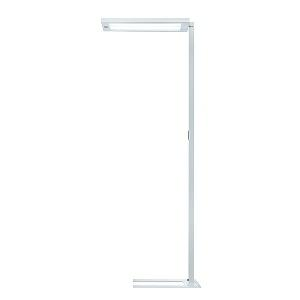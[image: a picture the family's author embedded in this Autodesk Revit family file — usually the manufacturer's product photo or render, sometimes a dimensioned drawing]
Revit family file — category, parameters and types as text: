
# Revit family: lavigo_-_dps_12000_840_r_g2_00741857_541e
name_source: partatom
category: Lighting Fixtures
units: mm (PartAtom-declared; Revit-internal decimal feet)

## family parameters
Cut with Voids When Loaded = No
Host = Face
Light Source = No
Part Type = Normal
Room Calculation Point = No
Round Connector Dimension = Use Diameter
Shared = No

## types (1)
- LAVIGO - DPS 12000/840/R/G2 (1 x LED, 11650 lm, 4000K)
    Apparent Load = 77 VA
    Approval mark = CE
    CIE Flux Codes = 60 87 97 15 100
    Color Rendering = 80-89
    Color Temperature = 4000K
    Control Gear = Electronic ballast
    Default Elevation = 1800 mm
    Description = DPS 12000/840/R/G2|Free-standing luminaire|light source: LED|work equipment: Electronic ballast|connected load: 220-240 V, 50/60 Hz|Power consumption: approx. 77 W|standby: approx. 0,50|power factor: approx. 0,930|luminous flux: 11650 lm|luminous efficacy: 151 lm/W|light distribution: Direct/indirect|direct ratio: approx. 15 %|colour temperature: Cold white, ca. 4000 K|color rendering index (CRI): >= 80|chromaticity tolerance:  3 SDCM|technology: Presence and daylight sensor control (PIR)|operation: Multi-function switch|luminaire body|material: Steel/plastic|surface: Painted|colour: White|lamp cover: Acrylic (PMMA), Satine|tubular section|material: Steel tube|surface: Painted|Form: Tubular section upright|colour of tubular section: White|luminaire base|Form: C-form flat|weight (net): approx. 19.7 kg|mains lead: 3.00 m Mains plug CEE 7/VII|Fastening: Floor standing base|decorative contrast side parts: Flint grey|glare control: Prism aperture|luminance(L65): <= 3000 cd/m|unified glare rating(4H 8H): <=  16|special features: Luminaire head detachable, Cradle to Cradle Certified TM, Direct light component with edge light and light-guide technology for homogenous light exit, Flicker-free, Integrated light and presence sensor PIR, Retrofittable with TALK module, Separated, direct and indirect light individually adjustable|Approval mark: VDE - ENEC|
    Frequency = 50 Hz
    Height = 36 mm
    Lamp = 1 x LED
    Lamp Light Flux = 11650 lm
    Lamp count = 1
    Length = 675 mm
    Luminous efficacy = 151 lm/W
    Manufacturer = Waldmann
    ModVariant = No
    Model = 00741857
    Mounting Place = Floor
    Mounting Type = Freestanding
    Number of Poles = 1
    OnlyDefault = Yes
    Power Factor = 1
    Product Name = LAVIGO - DPS 12000/840/R/G2
    Product group = Free standing luminaire
    ProductGroupID = 13
    Protection Class = Protection class I
    Protection Degree = IP 20
    RLX_Detail_Level = 1
    RLX_Emergency_Light_Flux = 0 lm
    RLX_Emergency_Type = 0
    RLX_Emergency_Type_DB = No
    RlxData = <blob elided: 37545 chars, md5=93db7b0a>
    Socket = socket
    Standby Power = 0 W
    System Light Flux = 11650 lm
    System Power = 77 W
    Type Comments = Product without accessories
    Type Image = 121695000-00610208.jpg
    URL = http://relux.com
    VarID = ---
    Voltage = 230 V
    Voltage Range = 220-240 V
    Weight = 0.00 kg
    Width = 320 mm

## geometry (parser evidence)
native form markers: Blend x4, Sweep x15
no freeform markers — native parametric forms only
